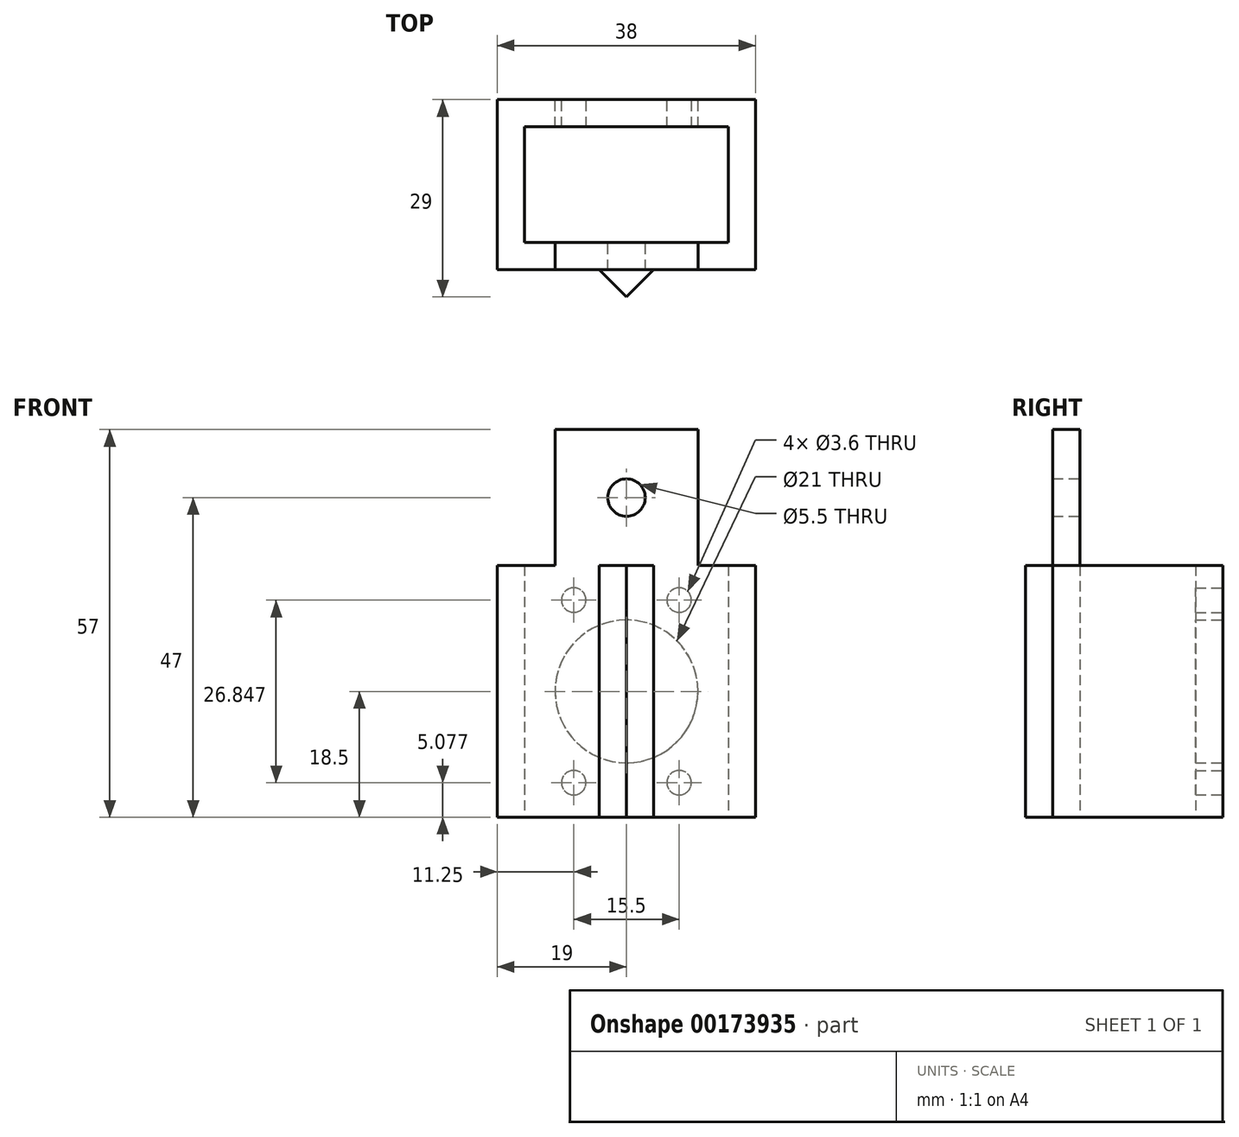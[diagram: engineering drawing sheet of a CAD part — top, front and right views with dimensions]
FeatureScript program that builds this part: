
annotation { "Feature Type Name" : "Feature", "Feature Type Description" : "" }
export const myFeature = defineFeature(function(context is Context, id is Id, definition is map)
    precondition{}
    {
        {
            var Q0;
            Q0=qCreatedBy(makeId("Top.planeOp"),FACE);
            var sketch = newSketch(context, id + "F0", { "sketchPlane" : qUnion([Q0])});
            skLineSegment(sketch, "E0.bottom", {"start": v(-13.5, 0) * mm, "end": v(13.5, 0) * mm});
            skLineSegment(sketch, "E0.top", {"start": v(-13.5, 27) * mm, "end": v(13.5, 27) * mm});
            skLineSegment(sketch, "E0.left", {"start": v(-13.5, 0) * mm, "end": v(-13.5, 27) * mm});
            skLineSegment(sketch, "E0.right", {"start": v(13.5, 0) * mm, "end": v(13.5, 27) * mm});
            skLineSegment(sketch, "E1.top", {"start": v(5, 0) * mm, "end": v(-5, 0) * mm});
            skSolve(sketch);
        }
        {
            var Q0;
            Q0=makeQuery(id+"F0.imprint","IMPRINT",FACE,{"disambiguationData":[TD([[makeQuery(id+"F0.imprint","IMPRINT",EDGE,{"derivedFrom":sQuery(id+"F0.wireOp",EDGE,"E0.bottom")}),1.0]])]});
            var Q1;
            Q1=makeQuery(id+"F0.imprint","IMPRINT",FACE,{"disambiguationData":[TD([[makeQuery(id+"F0.imprint","IMPRINT",EDGE,{"derivedFrom":sQuery(id+"F0.wireOp",EDGE,"E0.top")}),-1.0]])]});
            var Q2;
            Q2=makeQuery(id+"F0.imprint","IMPRINT",FACE,{"disambiguationData":[TD([[makeQuery(id+"F0.imprint","IMPRINT",EDGE,{"derivedFrom":sQuery(id+"F0.wireOp",EDGE,"r3kg0mCG-5yas-oTOn-g2Uv-CVAxs1bjjsDR.top")}),-1.0]])]});
            extrude(context, id + "F1", {"entities" : qUnion([Q0, Q1, Q2]), "depth" : 37 * mm, "offsetDistance" : 25 * mm});
        }
        {
            var Q0;
            Q0=makeQuery(id+"F1.opExtrude","CAP_FACE",FACE,{"disambiguationData":[OSD([sQuery(id+"F0.wireOp",EDGE,"E0.bottom"),sQuery(id+"F0.wireOp",EDGE,"E0.top"),sQuery(id+"F0.wireOp",EDGE,"E0.left"),sQuery(id+"F0.wireOp",EDGE,"E0.right")])],"isStart":false});
            var sketch = newSketch(context, id + "F2", { "sketchPlane" : qUnion([Q0])});
            skLineSegment(sketch, "E2", {"start": v(0, 27) * mm, "end": v(0, 0) * mm});
            skLineSegment(sketch, "E3", {"start": v(-13.5, 15.5) * mm, "end": v(13.5, 15.5) * mm});
            skLineSegment(sketch, "E4.bottom", {"start": v(10.5, 26) * mm, "end": v(-10.5, 26) * mm});
            skLineSegment(sketch, "E4.top", {"start": v(10.5, 5) * mm, "end": v(-10.5, 5) * mm});
            skLineSegment(sketch, "E4.left", {"start": v(10.5, 26) * mm, "end": v(10.5, 5) * mm});
            skLineSegment(sketch, "E4.right", {"start": v(-10.5, 26) * mm, "end": v(-10.5, 5) * mm});
            skPoint(sketch, "E4.middle", {"position": v(0, 15.5) * mm});
            skLineSegment(sketch, "E5", {"start": v(0, 9) * mm, "end": v(-4, 5) * mm});
            skLineSegment(sketch, "E6", {"start": v(0, 9) * mm, "end": v(4, 5) * mm});
            skLineSegment(sketch, "E7.1.0", {"start": v(6.5, 15.5) * mm, "end": v(10.5, 19.5) * mm});
            skLineSegment(sketch, "E7.1.1", {"start": v(6.5, 15.5) * mm, "end": v(10.5, 11.5) * mm});
            skLineSegment(sketch, "E7.2.0", {"start": v(0, 22) * mm, "end": v(-4, 26) * mm});
            skLineSegment(sketch, "E7.2.1", {"start": v(0, 22) * mm, "end": v(4, 26) * mm});
            skLineSegment(sketch, "E7.3.0", {"start": v(-6.5, 15.5) * mm, "end": v(-10.5, 11.5) * mm});
            skLineSegment(sketch, "E7.3.1", {"start": v(-6.5, 15.5) * mm, "end": v(-10.5, 19.5) * mm});
            skSolve(sketch);
        }
        {
            var Q0;
            {var subQ4=sQuery(id+"F2.wireOp",EDGE,"E7.2.0");Q0=makeQuery(id+"F2.imprint","IMPRINT",FACE,{"disambiguationData":[TD([[makeQuery(id+"F2.imprint","IMPRINT",EDGE,{"derivedFrom":subQ4}),1.0]])]});}
            var Q1;
            {var subQ3=sQuery(id+"F2.wireOp",EDGE,"E7.1.0");Q1=makeQuery(id+"F2.imprint","IMPRINT",FACE,{"disambiguationData":[TD([[makeQuery(id+"F2.imprint","IMPRINT",EDGE,{"derivedFrom":subQ3}),1.0]])]});}
            var Q2;
            {var subQ3=sQuery(id+"F2.wireOp",EDGE,"E6");Q2=makeQuery(id+"F2.imprint","IMPRINT",FACE,{"disambiguationData":[TD([[makeQuery(id+"F2.imprint","IMPRINT",EDGE,{"derivedFrom":subQ3}),1.0]])]});}
            var Q3;
            {var subQ4=sQuery(id+"F2.wireOp",EDGE,"E5");Q3=makeQuery(id+"F2.imprint","IMPRINT",FACE,{"disambiguationData":[TD([[makeQuery(id+"F2.imprint","IMPRINT",EDGE,{"derivedFrom":subQ4}),-1.0]])]});}
            var Q4;
            {var subQ0=sQuery(id+"F2.wireOp",EDGE,"E5");Q4=makeQuery(id+"F2.imprint","IMPRINT",FACE,{"disambiguationData":[TD([[makeQuery(id+"F2.imprint","IMPRINT",EDGE,{"derivedFrom":subQ0}),1.0]])]});}
            var Q5;
            {var subQ0=sQuery(id+"F2.wireOp",EDGE,"E6");Q5=makeQuery(id+"F2.imprint","IMPRINT",FACE,{"disambiguationData":[TD([[makeQuery(id+"F2.imprint","IMPRINT",EDGE,{"derivedFrom":subQ0}),-1.0]])]});}
            extrude(context, id + "F3", {"entities" : qUnion([Q0, Q1, Q2, Q3, Q4, Q5]), "operationType" : NewBodyOperationType.REMOVE, "endBound" : BoundingType.THROUGH_ALL, "oppositeDirection" : true, "depth" : 25 * mm, "offsetDistance" : 25 * mm});
        }
        {
            var Q0;
            Q0=qCreatedBy(makeId("Top.planeOp"),FACE);
            var sketch = newSketch(context, id + "F4", { "sketchPlane" : qUnion([Q0])});
            skLineSegment(sketch, "E8", {"start": v(0, 0) * mm, "end": v(0, 36.44) * mm});
            skLineSegment(sketch, "E9.bottom", {"start": v(-19, 0) * mm, "end": v(19, 0) * mm});
            skLineSegment(sketch, "E9.top", {"start": v(-19, 51) * mm, "end": v(19, 51) * mm});
            skLineSegment(sketch, "E9.left", {"start": v(-19, 0) * mm, "end": v(-19, 51) * mm});
            skLineSegment(sketch, "E9.right", {"start": v(19, 0) * mm, "end": v(19, 51) * mm});
            skLineSegment(sketch, "E10.bottom", {"start": v(15, 30) * mm, "end": v(-15, 30) * mm});
            skLineSegment(sketch, "E10.top", {"start": v(15, 47) * mm, "end": v(-15, 47) * mm});
            skLineSegment(sketch, "E10.left", {"start": v(15, 30) * mm, "end": v(15, 47) * mm});
            skLineSegment(sketch, "E10.right", {"start": v(-15, 30) * mm, "end": v(-15, 47) * mm});
            skPoint(sketch, "E10.middle", {"position": v(0, 38.5) * mm});
            skLineSegment(sketch, "E11.bottom", {"start": v(-13.5, 0) * mm, "end": v(13.5, 0) * mm});
            skLineSegment(sketch, "E11.top", {"start": v(-13.5, 27) * mm, "end": v(13.5, 27) * mm});
            skLineSegment(sketch, "E11.left", {"start": v(-13.5, 0) * mm, "end": v(-13.5, 27) * mm});
            skLineSegment(sketch, "E11.right", {"start": v(13.5, 0) * mm, "end": v(13.5, 27) * mm});
            skSolve(sketch);
        }
        {
            var Q0;
            {var subQ6=sQuery(id+"F4.wireOp",EDGE,"rIE9HAYr-Mk53-lMAW-OUrn-GBfFgdMOiOzT");Q0=makeQuery(id+"F4.imprint","IMPRINT",FACE,{"disambiguationData":[TD([[makeQuery(id+"F4.imprint","IMPRINT",EDGE,{"derivedFrom":subQ6}),-1.0]])]});}
            var Q1;
            {var subQ0=sQuery(id+"F4.wireOp",EDGE,"6CUglaKy-5Dma-Ekc3-7SDl-NO9MYHuwZmba");Q1=makeQuery(id+"F4.imprint","IMPRINT",FACE,{"disambiguationData":[TD([[makeQuery(id+"F4.imprint","IMPRINT",EDGE,{"derivedFrom":subQ0}),1.0]])]});}
            var Q2;
            {var subQ9=sQuery(id+"F4.wireOp",EDGE,"oW8Bx6Ec-5IkK-D0za-Qmyw-sU9NhfovICgU");Q2=makeQuery(id+"F4.imprint","IMPRINT",FACE,{"disambiguationData":[TD([[makeQuery(id+"F4.imprint","IMPRINT",EDGE,{"derivedFrom":subQ9}),-1.0]])]});}
            var Q3;
            {var subQ0=sQuery(id+"F4.wireOp",EDGE,"4FIgG3Di-sbtT-Y5dX-kcbB-M1VmEsIUGLha");Q3=makeQuery(id+"F4.imprint","IMPRINT",FACE,{"disambiguationData":[TD([[makeQuery(id+"F4.imprint","IMPRINT",EDGE,{"derivedFrom":subQ0}),-1.0]])]});}
            var Q4;
            Q4=makeQuery(id+"F4.imprint","IMPRINT",FACE,{"disambiguationData":[TD([[makeQuery(id+"F4.imprint","IMPRINT",EDGE,{"derivedFrom":sQuery(id+"F4.wireOp",EDGE,"E9.top")}),-1.0]])]});
            var Q5;
            Q5=makeQuery(id+"F1.opExtrude","CAP_FACE",FACE,{"disambiguationData":[OSD([sQuery(id+"F0.wireOp",EDGE,"E0.top"),sQuery(id+"F0.wireOp",EDGE,"E0.left"),sQuery(id+"F0.wireOp",EDGE,"E0.right"),sQuery(id+"F0.wireOp",EDGE,"r3kg0mCG-5yas-oTOn-g2Uv-CVAxs1bjjsDR.bottom"),sQuery(id+"F0.wireOp",EDGE,"r3kg0mCG-5yas-oTOn-g2Uv-CVAxs1bjjsDR.top"),sQuery(id+"F0.wireOp",EDGE,"r3kg0mCG-5yas-oTOn-g2Uv-CVAxs1bjjsDR.left"),sQuery(id+"F0.wireOp",EDGE,"r3kg0mCG-5yas-oTOn-g2Uv-CVAxs1bjjsDR.right"),sQuery(id+"F0.wireOp",EDGE,"E1.top"),sQuery(id+"F0.wireOp",EDGE,"E1.left"),sQuery(id+"F0.wireOp",EDGE,"E1.right")])],"isStart":false});
            extrude(context, id + "F5", {"entities" : qUnion([Q0, Q1, Q2, Q3, Q4]), "operationType" : NewBodyOperationType.ADD, "endBound" : BoundingType.UP_TO_SURFACE, "depth" : 25 * mm, "endBoundEntityFace" : qUnion([Q5]), "offsetDistance" : 25 * mm});
        }
        {
            var Q0;
            Q0=makeQuery(id+"F5.opExtrude","SWEPT_FACE",FACE,{"disambiguationData":[OSD([sQuery(id+"F4.wireOp",EDGE,"E9.top")])]});
            var sketch = newSketch(context, id + "F6", { "sketchPlane" : qUnion([Q0])});
            skLineSegment(sketch, "E12", {"start": v(-19, 18.5) * mm, "end": v(19, 18.5) * mm});
            skLineSegment(sketch, "E13", {"start": v(0, 37) * mm, "end": v(0, 0) * mm});
            skPoint(sketch, "E14.middle", {"position": v(0, 18.5) * mm});
            skPoint(sketch, "E15", {"position": v(15.5, 18.5) * mm});
            skPoint(sketch, "E16.1.0", {"position": v(7.75, 31.92) * mm});
            skPoint(sketch, "E16.2.0", {"position": v(-7.75, 31.92) * mm});
            skPoint(sketch, "E16.3.0", {"position": v(-15.5, 18.5) * mm});
            skPoint(sketch, "E16.4.0", {"position": v(-7.75, 5.08) * mm});
            skPoint(sketch, "E16.5.0", {"position": v(7.75, 5.08) * mm});
            skSolve(sketch);
        }
        {
            var Q0;
            Q0=sQuery(id+"F6.wireOp",VERTEX,"E16.4.0");
            var Q1;
            Q1=sQuery(id+"F6.wireOp",VERTEX,"E16.5.0");
            var Q2;
            Q2=sQuery(id+"F6.wireOp",VERTEX,"E16.1.0");
            var Q3;
            Q3=sQuery(id+"F6.wireOp",VERTEX,"E16.2.0");
            var Q4;
            Q4=makeQuery(id+"F1.opExtrude","SWEPT_BODY",BODY,{"disambiguationData":[OSD([sQuery(id+"F0.wireOp",EDGE,"E0.top"),sQuery(id+"F0.wireOp",EDGE,"E0.left"),sQuery(id+"F0.wireOp",EDGE,"E0.right"),sQuery(id+"F0.wireOp",EDGE,"r3kg0mCG-5yas-oTOn-g2Uv-CVAxs1bjjsDR.bottom"),sQuery(id+"F0.wireOp",EDGE,"r3kg0mCG-5yas-oTOn-g2Uv-CVAxs1bjjsDR.top"),sQuery(id+"F0.wireOp",EDGE,"r3kg0mCG-5yas-oTOn-g2Uv-CVAxs1bjjsDR.left"),sQuery(id+"F0.wireOp",EDGE,"r3kg0mCG-5yas-oTOn-g2Uv-CVAxs1bjjsDR.right"),sQuery(id+"F0.wireOp",EDGE,"E1.top"),sQuery(id+"F0.wireOp",EDGE,"E1.left"),sQuery(id+"F0.wireOp",EDGE,"E1.right")])]});
            hole(context, id + "F7", {"style" : HoleStyle.SIMPLE, "endStyle" : HoleEndStyle.BLIND, "standardTappedOrClearance" : lookupTablePath({ "fit" : "Loose", "standard" : "ISO", "size" : "M3", "type" : "Clearance" }), "standardBlindInLast" : lookupTablePath({ "fit" : "Loose", "standard" : "ISO", "engagement" : "75%", "pitch" : "0.5 mm", "size" : "M3", "type" : "Clearance & tapped" }), "holeDiameter" : 3.6 * mm, "majorDiameter" : 5 * mm, "holeDepth" : 10 * mm, "tappedDepth" : 12 * mm, "tapClearance" : 3, "locations" : qUnion([Q0, Q1, Q2, Q3]), "scope" : qUnion([Q4])});
        }
        {
            var Q0;
            Q0=sQuery(id+"F6.wireOp",VERTEX,"E14.middle");
            var Q1;
            Q1=makeQuery(id+"F1.opExtrude","SWEPT_BODY",BODY,{"disambiguationData":[OSD([sQuery(id+"F0.wireOp",EDGE,"E0.top"),sQuery(id+"F0.wireOp",EDGE,"E0.left"),sQuery(id+"F0.wireOp",EDGE,"E0.right"),sQuery(id+"F0.wireOp",EDGE,"r3kg0mCG-5yas-oTOn-g2Uv-CVAxs1bjjsDR.bottom"),sQuery(id+"F0.wireOp",EDGE,"r3kg0mCG-5yas-oTOn-g2Uv-CVAxs1bjjsDR.top"),sQuery(id+"F0.wireOp",EDGE,"r3kg0mCG-5yas-oTOn-g2Uv-CVAxs1bjjsDR.left"),sQuery(id+"F0.wireOp",EDGE,"r3kg0mCG-5yas-oTOn-g2Uv-CVAxs1bjjsDR.right"),sQuery(id+"F0.wireOp",EDGE,"E1.top"),sQuery(id+"F0.wireOp",EDGE,"E1.left"),sQuery(id+"F0.wireOp",EDGE,"E1.right")])]});
            hole(context, id + "F8", {"style" : HoleStyle.SIMPLE, "endStyle" : HoleEndStyle.BLIND, "holeDiameter" : 21 * mm, "majorDiameter" : 5 * mm, "holeDepth" : 10 * mm, "tappedDepth" : 12 * mm, "tapClearance" : 3, "locations" : qUnion([Q0]), "scope" : qUnion([Q1])});
        }
        {
            var Q0;
            Q0=makeQuery(id+"F5.boolean.opBoolean","MERGE",FACE,{"derivedFrom":[makeQuery(id+"F1.opExtrude","CAP_FACE",FACE,{"disambiguationData":[OSD([sQuery(id+"F0.wireOp",EDGE,"E0.bottom"),sQuery(id+"F0.wireOp",EDGE,"E0.top"),sQuery(id+"F0.wireOp",EDGE,"E0.left"),sQuery(id+"F0.wireOp",EDGE,"E0.right"),sQuery(id+"F0.wireOp",EDGE,"E1.top")])],"isStart":false}),makeQuery(id+"F5.opExtrude","CAP_FACE",FACE,{"disambiguationData":[OSD([sQuery(id+"F4.wireOp",EDGE,"E9.bottom"),sQuery(id+"F4.wireOp",EDGE,"E9.top"),sQuery(id+"F4.wireOp",EDGE,"E9.left"),sQuery(id+"F4.wireOp",EDGE,"E9.right"),sQuery(id+"F4.wireOp",EDGE,"E10.bottom"),sQuery(id+"F4.wireOp",EDGE,"E10.top"),sQuery(id+"F4.wireOp",EDGE,"E10.left"),sQuery(id+"F4.wireOp",EDGE,"E10.right"),sQuery(id+"F4.wireOp",EDGE,"E11.top"),sQuery(id+"F4.wireOp",EDGE,"E11.left"),sQuery(id+"F4.wireOp",EDGE,"E11.right")])],"isStart":false})]});
            var sketch = newSketch(context, id + "F9", { "sketchPlane" : qUnion([Q0])});
            skLineSegment(sketch, "E17.bottom", {"start": v(-19, 0) * mm, "end": v(-5.5, 0) * mm});
            skLineSegment(sketch, "E17.top", {"start": v(-19, 26) * mm, "end": v(-5.5, 26) * mm});
            skLineSegment(sketch, "E17.left", {"start": v(-19, 0) * mm, "end": v(-19, 26) * mm});
            skLineSegment(sketch, "E17.right", {"start": v(-5.5, 0) * mm, "end": v(-5.5, 26) * mm});
            skLineSegment(sketch, "E18.bottom", {"start": v(19, 0) * mm, "end": v(5.5, 0) * mm});
            skLineSegment(sketch, "E18.top", {"start": v(19, 26) * mm, "end": v(5.5, 26) * mm});
            skLineSegment(sketch, "E18.left", {"start": v(19, 0) * mm, "end": v(19, 26) * mm});
            skLineSegment(sketch, "E18.right", {"start": v(5.5, 0) * mm, "end": v(5.5, 26) * mm});
            skLineSegment(sketch, "E19.bottom", {"start": v(-5.5, 8.97) * mm, "end": v(5.5, 8.97) * mm});
            skLineSegment(sketch, "E19.top", {"start": v(-5.5, 0) * mm, "end": v(5.5, 0) * mm});
            skLineSegment(sketch, "E19.left", {"start": v(-5.5, 8.97) * mm, "end": v(-5.5, 0) * mm});
            skLineSegment(sketch, "E19.right", {"start": v(5.5, 8.97) * mm, "end": v(5.5, 0) * mm});
            skSolve(sketch);
        }
        {
            var Q0;
            Q0=makeQuery(id+"F9.imprint","IMPRINT",FACE,{"disambiguationData":[TD([[makeQuery(id+"F9.imprint","IMPRINT",EDGE,{"derivedFrom":sQuery(id+"F9.wireOp",EDGE,"E17.bottom")}),1.0]])]});
            var Q1;
            Q1=makeQuery(id+"F9.imprint","IMPRINT",FACE,{"disambiguationData":[TD([[makeQuery(id+"F9.imprint","IMPRINT",EDGE,{"derivedFrom":sQuery(id+"F9.wireOp",EDGE,"E18.bottom")}),1.0]])]});
            var Q2;
            {var subQ0=sQuery(id+"F9.wireOp",EDGE,"E19.top");Q2=makeQuery(id+"F9.imprint","IMPRINT",FACE,{"disambiguationData":[TD([[makeQuery(id+"F9.imprint","IMPRINT",EDGE,{"derivedFrom":subQ0}),1.0]])]});}
            extrude(context, id + "F10", {"entities" : qUnion([Q0, Q1, Q2]), "operationType" : NewBodyOperationType.REMOVE, "endBound" : BoundingType.THROUGH_ALL, "oppositeDirection" : true, "depth" : 25 * mm, "offsetDistance" : 25 * mm});
        }
        {
            var Q0;
            Q0=makeQuery(id+"F5.boolean.opBoolean","MERGE",FACE,{"derivedFrom":[makeQuery(id+"F1.opExtrude","CAP_FACE",FACE,{"disambiguationData":[OSD([sQuery(id+"F0.wireOp",EDGE,"E0.bottom"),sQuery(id+"F0.wireOp",EDGE,"E0.top"),sQuery(id+"F0.wireOp",EDGE,"E0.left"),sQuery(id+"F0.wireOp",EDGE,"E0.right"),sQuery(id+"F0.wireOp",EDGE,"E1.top")])],"isStart":false}),makeQuery(id+"F5.opExtrude","CAP_FACE",FACE,{"disambiguationData":[OSD([sQuery(id+"F4.wireOp",EDGE,"E9.bottom"),sQuery(id+"F4.wireOp",EDGE,"E9.top"),sQuery(id+"F4.wireOp",EDGE,"E9.left"),sQuery(id+"F4.wireOp",EDGE,"E9.right"),sQuery(id+"F4.wireOp",EDGE,"E10.bottom"),sQuery(id+"F4.wireOp",EDGE,"E10.top"),sQuery(id+"F4.wireOp",EDGE,"E10.left"),sQuery(id+"F4.wireOp",EDGE,"E10.right"),sQuery(id+"F4.wireOp",EDGE,"E11.top"),sQuery(id+"F4.wireOp",EDGE,"E11.left"),sQuery(id+"F4.wireOp",EDGE,"E11.right")])],"isStart":false})]});
            var sketch = newSketch(context, id + "F11", { "sketchPlane" : qUnion([Q0])});
            skLineSegment(sketch, "E20.bottom", {"start": v(10.5, 26) * mm, "end": v(-10.5, 26) * mm});
            skLineSegment(sketch, "E20.top", {"start": v(10.5, 30) * mm, "end": v(-10.5, 30) * mm});
            skLineSegment(sketch, "E20.left", {"start": v(10.5, 26) * mm, "end": v(10.5, 30) * mm});
            skLineSegment(sketch, "E20.right", {"start": v(-10.5, 26) * mm, "end": v(-10.5, 30) * mm});
            skPoint(sketch, "E20.middle", {"position": v(0, 28) * mm});
            skLineSegment(sketch, "E21", {"start": v(-19, 28) * mm, "end": v(19, 28) * mm});
            skSolve(sketch);
        }
        {
            var Q0;
            Q0 = qSketchRegion(id + "F11", true);
            var Q1;
            {var subQ1=sQuery(id+"F11.wireOp",EDGE,"E20.bottom");var subQ7=sQuery(id+"F2.wireOp",EDGE,"E7.2.0");var subQ8=makeQuery(id+"F11.imprint","INTERSECT",VERTEX,{"derivedFrom":[makeQuery(id+"F3.boolean.opBoolean","COPY",EDGE,{"derivedFrom":makeQuery(id+"F3.opExtrude","CAP_EDGE",EDGE,{"disambiguationData":[OSD([subQ7])],"isStart":true})}),subQ1]});Q1=makeQuery(id+"F11.imprint","IMPRINT",FACE,{"disambiguationData":[TD([[makeQuery(id+"F11.imprint","IMPRINT",EDGE,{"disambiguationData":[TD([[subQ8,1.0]])],"derivedFrom":subQ1}),-1.0]])]});}
            extrude(context, id + "F12", {"entities" : qUnion([Q0, Q1]), "operationType" : NewBodyOperationType.ADD, "depth" : 20 * mm, "offsetDistance" : 25 * mm});
        }
        {
            var Q0;
            Q0=makeQuery(id+"F12.boolean.opBoolean","MERGE",FACE,{"derivedFrom":[makeQuery(id+"F5.opExtrude","SWEPT_FACE",FACE,{"disambiguationData":[OSD([sQuery(id+"F4.wireOp",EDGE,"E10.bottom")])]}),makeQuery(id+"F12.opExtrude","SWEPT_FACE",FACE,{"disambiguationData":[OSD([sQuery(id+"F11.wireOp",EDGE,"E20.top")])]})]});
            var sketch = newSketch(context, id + "F13", { "sketchPlane" : qUnion([Q0])});
            skLineSegment(sketch, "E22.bottom", {"start": v(10.5, 37) * mm, "end": v(-10.5, 37) * mm});
            skLineSegment(sketch, "E22.top", {"start": v(10.5, 57) * mm, "end": v(-10.5, 57) * mm});
            skLineSegment(sketch, "E22.left", {"start": v(10.5, 37) * mm, "end": v(10.5, 57) * mm});
            skLineSegment(sketch, "E22.right", {"start": v(-10.5, 37) * mm, "end": v(-10.5, 57) * mm});
            skPoint(sketch, "E22.middle", {"position": v(0, 47) * mm});
            skSolve(sketch);
        }
        {
            var Q0;
            Q0=sQuery(id+"F13.wireOp",VERTEX,"E22.middle");
            var Q1;
            Q1=makeQuery(id+"F1.opExtrude","SWEPT_BODY",BODY,{"disambiguationData":[OSD([sQuery(id+"F0.wireOp",EDGE,"xHkcvzyH-9kmu-wbCr-jR9n-D6HEL6nOpGrQ"),sQuery(id+"F0.wireOp",EDGE,"HCY4NaYE-prSY-boik-VQEE-KTlIMcDiN2et"),sQuery(id+"F0.wireOp",EDGE,"WuNqzkiV-5fIL-Ygxi-hsma-e7T6jagV0e0Y"),sQuery(id+"F0.wireOp",EDGE,"2OK0SqrW-3Etj-5ayL-7rRH-hWcyb4yQmMM4"),sQuery(id+"F0.wireOp",EDGE,"lwhvDbMa-AmNj-0qt0-y0KF-N0vn7AxuHUuw"),sQuery(id+"F0.wireOp",EDGE,"Bpkg6DPL-H1ym-XptN-jvIf-c3K8TXIWIoFH"),sQuery(id+"F0.wireOp",EDGE,"hlCVzPfB-2dpC-Jpgm-U181-AJxs24huhhLZ"),sQuery(id+"F0.wireOp",EDGE,"8QqTi3ct-ThRm-gueO-aHDC-F4Muzk4KxUct.top"),sQuery(id+"F0.wireOp",EDGE,"8QqTi3ct-ThRm-gueO-aHDC-F4Muzk4KxUct.left"),sQuery(id+"F0.wireOp",EDGE,"8QqTi3ct-ThRm-gueO-aHDC-F4Muzk4KxUct.right"),sQuery(id+"F0.wireOp",EDGE,"d1653463-5d28-4219-b4a5-8c73052c44480.MirrorCS"),sQuery(id+"F0.wireOp",EDGE,"8604e583-d332-466a-8dde-0e841fae2b530.MirrorCS"),sQuery(id+"F0.wireOp",EDGE,"2614f8c5-c022-48f9-b6df-9e0814651a8c0.MirrorCS"),sQuery(id+"F0.wireOp",EDGE,"EvqpzCpu-QXtl-eKPM-fO3z-jtB7Z1EKyX8v"),sQuery(id+"F0.wireOp",EDGE,"TuMM16le-KGyB-roy2-t4tL-9nZMhsLml1HU")])]});
            var Q2;
            Q2=makeQuery(id+"F1.opExtrude","SWEPT_BODY",BODY,{"disambiguationData":[OSD([sQuery(id+"F0.wireOp",EDGE,"E0.top"),sQuery(id+"F0.wireOp",EDGE,"E0.left"),sQuery(id+"F0.wireOp",EDGE,"E0.right"),sQuery(id+"F0.wireOp",EDGE,"r3kg0mCG-5yas-oTOn-g2Uv-CVAxs1bjjsDR.bottom"),sQuery(id+"F0.wireOp",EDGE,"r3kg0mCG-5yas-oTOn-g2Uv-CVAxs1bjjsDR.top"),sQuery(id+"F0.wireOp",EDGE,"r3kg0mCG-5yas-oTOn-g2Uv-CVAxs1bjjsDR.left"),sQuery(id+"F0.wireOp",EDGE,"r3kg0mCG-5yas-oTOn-g2Uv-CVAxs1bjjsDR.right"),sQuery(id+"F0.wireOp",EDGE,"E1.top"),sQuery(id+"F0.wireOp",EDGE,"E1.left"),sQuery(id+"F0.wireOp",EDGE,"E1.right")])]});
            hole(context, id + "F14", {"style" : HoleStyle.SIMPLE, "endStyle" : HoleEndStyle.BLIND, "standardTappedOrClearance" : lookupTablePath({ "standard" : "ISO", "fit" : "Normal", "size" : "M5", "type" : "Clearance" }), "standardBlindInLast" : lookupTablePath({ "fit" : "Standard", "standard" : "ISO", "size" : "M5", "type" : "Clearance" }), "holeDiameter" : 5.5 * mm, "majorDiameter" : 5 * mm, "holeDepth" : 12 * mm, "locations" : qUnion([Q0]), "scope" : qUnion([Q1, Q2]), "tappedDepth" : 12 * mm, "tapClearance" : 3});
        }
    });
